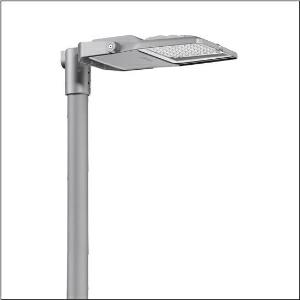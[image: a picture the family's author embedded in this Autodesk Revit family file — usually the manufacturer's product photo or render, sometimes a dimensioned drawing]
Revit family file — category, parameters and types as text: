
# Revit family: floodlight_fl_21_iq_mini___pl52_5xa7772d2d3a_9966
name_source: partatom
category: Lighting Fixtures
units: mm (PartAtom-declared; Revit-internal decimal feet)

## family parameters
Cut with Voids When Loaded = No
Host = Face
Light Source = No
Part Type = Normal
Room Calculation Point = No
Round Connector Dimension = Use Diameter
Shared = No

## types (1)
- --- (1 x LED, 17830 lm, 143 W, 3000K)
    Apparent Load = 143 VA
    CIE Flux Codes = 26 60 98 100 100
    Color Rendering = 70
    Color Temperature = 3000K
    Default Elevation = 1800 mm
    Description = Floodlight FL 21 iQ mini, floodlight, primary light control with lens, of PMMA, primary optical cover: protective disc, of toughened safety glass, transparent, light distribution: PL52, light emission: direct distribution, installation type: surface-mounted, LED, High Power LED, rated luminous flux: 17.830lm, luminous efficacy: 125lm/W, light colour: 730, colour temperature: 3000K, control: Auto-Match, Temp-Guard, Night-Set, Smart-Wire, Desk-Remote (wireless, voltage-free reading and setting of iQ features in the workshop via application-optimized NFC function/RFID function), optimised constant luminous flux control (CLO 2.0), Light-Fading, Lumen-Switch, with terminal, 6-pole, mains connection: 220..240V, AC, 50/60Hz, start of lifetime: 143W, end of service life: 152W, reduction: 61W, luminaire housing, of diecast aluminium, powder-coated, Siteco® metallic grey (DB 702S), corrosivity category C5 mid according to DIN EN ISO 12944, sealing non-destructively replaceable, please order mast flange separately, mast bracket, of steel, galvanised, powder-coated, protection rating (complete): IP66, insulation class (complete): insulation class II (safety insulation), certification: CE, ENEC, VDE, protection symbol: D, impact resistance: IK08, permissible operating ambient temperature: -40..+40°C, permissible operating ambient temperature for outdoor applications: -40..+50°C, standard: DIN EN 12944, LABS conformity tested according to VDMA 24364:2018-05, packaging unit: 1 piece

Light Distribution: PL52
    Height = 70 mm
    Lamp = 1 x LED
    Lamp Light Flux = 17830 lm
    Lamp Power = 143 W
    Lamp count = 1
    Length = 485 mm
    Luminous efficacy = 125 lm/W
    Manufacturer = Siteco
    ModVariant = No
    Model = 5XA7772D2D3A
    Number of Poles = 1
    OnlyDefault = Yes
    Power Factor = 1
    Product Name = Floodlight FL 21 iQ mini | PL52
    Product group = floodlight | pylon annexe
    ProductGroupID = 6200
    Protection Class = Protection class II
    Protection Degree = IP 66
    RLX_Detail_Level = 1
    RLX_Emergency_Light_Flux = 0 lm
    RLX_Emergency_Type = 0
    RLX_Emergency_Type_DB = No
    RlxData = <blob elided: 101901 chars, md5=11e27861>
    Socket = socket
    Standby Power = 0 W
    System Light Flux = 17830 lm
    System Power = 143 W
    Type Comments = factory setting: luminous flux: 100 % | dim-lin: 254 | 730 mA
    Type Image = l_1007125.jpg
    URL = http://relux.com
    VarID = @adj_134045
    Voltage = 0 V
    Weight = 0.00 kg
    Width = 337 mm

## geometry (parser evidence)
native form markers: Blend x4, Sweep x11
no freeform markers — native parametric forms only
